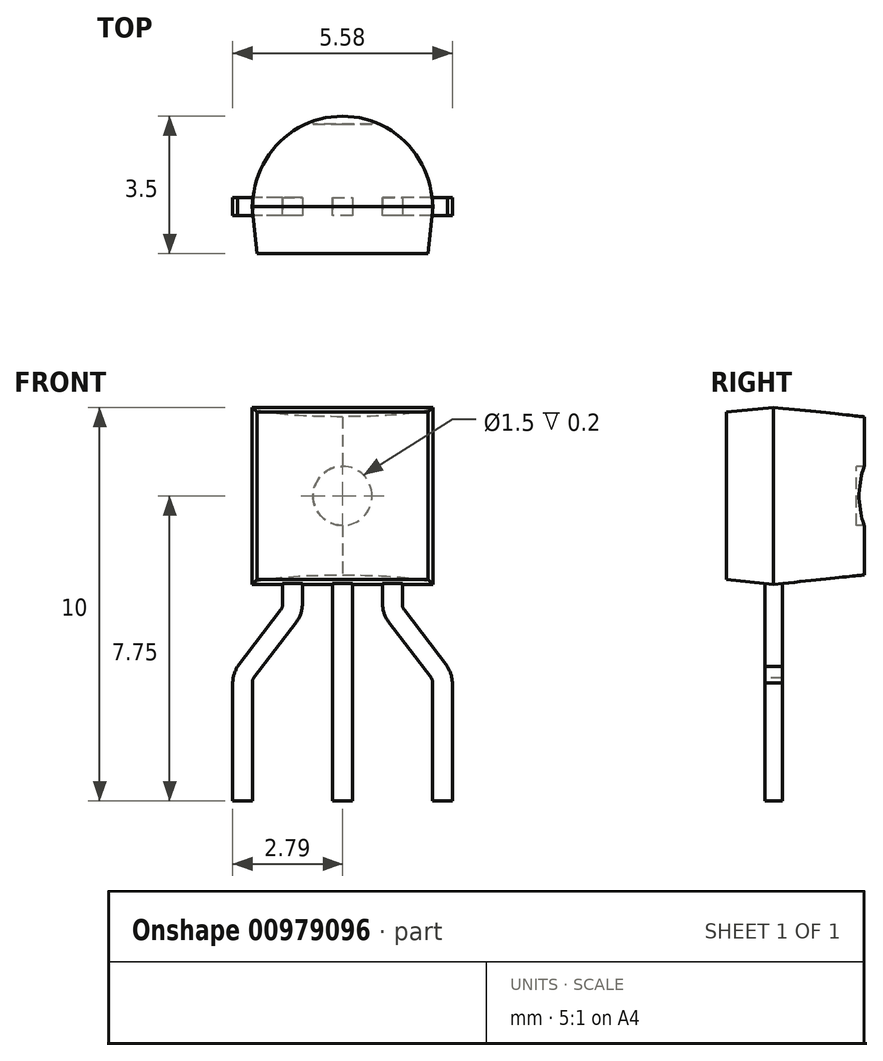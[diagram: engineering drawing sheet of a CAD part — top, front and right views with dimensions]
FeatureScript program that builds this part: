
annotation { "Feature Type Name" : "Feature", "Feature Type Description" : "" }
export const myFeature = defineFeature(function(context is Context, id is Id, definition is map)
    precondition{}
    {
        {
            assignVariable(context, id + "F0", {"name" : "A2", "anyValue" : 1.2});
        }
        {
            assignVariable(context, id + "F1", {"name" : "D", "anyValue" : 4.6});
        }
        {
            assignVariable(context, id + "F2", {"name" : "h", "anyValue" : 0.2});
        }
        {
            assignVariable(context, id + "F3", {"name" : "L1", "anyValue" : 3});
        }
        {
            var Q0;
            Q0=qCreatedBy(makeId("Front.planeOp"),FACE);
            var sketch = newSketch(context, id + "F4", { "sketchPlane" : qUnion([Q0])});
            skLineSegment(sketch, "E0.bottom", {"start": v(2.3, 0) * mm, "end": v(-2.3, 0) * mm});
            skLineSegment(sketch, "E0.top", {"start": v(2.3, 4.5) * mm, "end": v(-2.3, 4.5) * mm});
            skLineSegment(sketch, "E0.left", {"start": v(2.3, 0) * mm, "end": v(2.3, 4.5) * mm});
            skLineSegment(sketch, "E0.right", {"start": v(-2.3, 0) * mm, "end": v(-2.3, 4.5) * mm});
            skPoint(sketch, "E0.middle", {"position": v(0, 2.25) * mm});
            skSolve(sketch);
        }
        {
            var Q0;
            Q0=makeQuery(id+"F4.imprint","IMPRINT",FACE,{"disambiguationData":[TD([[makeQuery(id+"F4.imprint","IMPRINT",EDGE,{"derivedFrom":sQuery(id+"F4.wireOp",EDGE,"E0.bottom")}),-1.0]])]});
            extrude(context, id + "F5", {"entities" : qUnion([Q0]), "depth" : getVariable(context, 'A2') * mm, "offsetDistance" : 25 * mm, "hasDraft" : true, "draftAngle" : 6 * degree, "draftPullDirection" : true, "hasSecondDirection" : true, "secondDirectionOppositeDirection" : true, "secondDirectionDepth" : getVariable(context, 'D') / 2 * mm, "hasSecondDirectionDraft" : true, "secondDirectionDraftAngle" : 6 * degree, "secondDirectionDraftPullDirection" : true});
        }
        {
            var Q0;
            Q0=makeQuery(id+"F5.opExtrude","CAP_EDGE",EDGE,{"disambiguationData":[OSD([sQuery(id+"F4.wireOp",EDGE,"E0.right")])],"isStart":true});
            var Q1;
            Q1=makeQuery(id+"F5.opExtrude","CAP_EDGE",EDGE,{"disambiguationData":[OSD([sQuery(id+"F4.wireOp",EDGE,"E0.left")])],"isStart":true});
            fillet(context, id + "F6", {"entities" : qUnion([Q0, Q1]), "radius" : getVariable(context, 'D') / 2 * mm, "tangentPropagation" : true, "allowEdgeOverflow" : false});
        }
        {
            var Q0;
            Q0=makeQuery(id+"F5.opExtrude","CAP_FACE",FACE,{"disambiguationData":[OSD([sQuery(id+"F4.wireOp",EDGE,"E0.bottom"),sQuery(id+"F4.wireOp",EDGE,"E0.top"),sQuery(id+"F4.wireOp",EDGE,"E0.left"),sQuery(id+"F4.wireOp",EDGE,"E0.right")])],"isStart":false});
            var sketch = newSketch(context, id + "F7", { "sketchPlane" : qUnion([Q0])});
            skCircle(sketch, "E1", {"center": v(0, 2.25) * mm, "radius": 0.75 * mm});
            skPoint(sketch, "E1.centerSnap0", {"position": v(2.17, 2.25) * mm});
            skSolve(sketch);
        }
        {
            var Q0;
            Q0=makeQuery(id+"F7.imprint","IMPRINT",FACE,{"disambiguationData":[TD([[makeQuery(id+"F7.imprint","IMPRINT",EDGE,{"derivedFrom":sQuery(id+"F7.wireOp",EDGE,"E1")}),1.0]])]});
            extrude(context, id + "F8", {"entities" : qUnion([Q0]), "operationType" : NewBodyOperationType.REMOVE, "endBound" : BoundingType.THROUGH_ALL, "oppositeDirection" : true, "depth" : 25 * mm, "offsetDistance" : 25 * mm, "hasSecondDirection" : true, "secondDirectionOppositeDirection" : true, "secondDirectionDepth" : (getVariable(context, 'D') / 2 + getVariable(context, 'A2') - getVariable(context, 'h')) * mm});
        }
        {
            var Q0;
            Q0=qCreatedBy(makeId("Front.planeOp"),FACE);
            var sketch = newSketch(context, id + "F9", { "sketchPlane" : qUnion([Q0])});
            skLineSegment(sketch, "E2", {"start": v(0, 2.25) * mm, "end": v(-1.27, 2.25) * mm});
            skLineSegment(sketch, "E3", {"start": v(-2.54, -2.5) * mm, "end": v(-2.54, -5.5) * mm});
            skLineSegment(sketch, "E4", {"start": v(0, 2.25) * mm, "end": v(0, -5.5) * mm, "construction": true});
            skPoint(sketch, "E5.visualSharp", {"position": v(-2.54, -2.5) * mm});
            skArc(sketch, "E5.filletArc", {"start": v(-2.46, -2.23) * mm, "mid": v(-2.52, -2.36) * mm, "end": v(-2.54, -2.5) * mm});
            skLineSegment(sketch, "E6.MirrorCS", {"start": v(0, 2.25) * mm, "end": v(1.27, 2.25) * mm});
            skLineSegment(sketch, "E7.MirrorCS", {"start": v(1.27, 2.25) * mm, "end": v(1.27, -0.5) * mm});
            skLineSegment(sketch, "E8.MirrorCS", {"start": v(1.37, -0.8) * mm, "end": v(2.46, -2.23) * mm});
            skLineSegment(sketch, "E9.MirrorCS", {"start": v(2.54, -2.5) * mm, "end": v(2.54, -5.5) * mm});
            skArc(sketch, "E10.MirrorCS", {"start": v(2.46, -2.23) * mm, "mid": v(2.52, -2.36) * mm, "end": v(2.54, -2.5) * mm});
            skPoint(sketch, "E11.visualSharp", {"position": v(1.27, -0.67) * mm});
            skArc(sketch, "E11.filletArc", {"start": v(1.27, -0.5) * mm, "mid": v(1.3, -0.66) * mm, "end": v(1.37, -0.8) * mm});
            skLineSegment(sketch, "E12.MirrorCS", {"start": v(-1.27, 2.25) * mm, "end": v(-1.27, -0.5) * mm});
            skLineSegment(sketch, "E13.MirrorCS", {"start": v(-1.37, -0.8) * mm, "end": v(-2.46, -2.23) * mm});
            skArc(sketch, "E14.MirrorCS", {"start": v(-1.27, -0.5) * mm, "mid": v(-1.3, -0.66) * mm, "end": v(-1.37, -0.8) * mm});
            skSolve(sketch);
        }
        {
            var Q0;
            Q0=qCreatedBy(makeId("Right.planeOp"),FACE);
            var sketch = newSketch(context, id + "F10", { "sketchPlane" : qUnion([Q0])});
            skLineSegment(sketch, "E15", {"start": v(0, 2.25) * mm, "end": v(0, -0.5) * mm});
            skLineSegment(sketch, "E16", {"start": v(0, -0.5) * mm, "end": v(0, -2.5) * mm});
            skLineSegment(sketch, "E17", {"start": v(0, -2.5) * mm, "end": v(0, -5.5) * mm});
            skPoint(sketch, "E18.visualSharp", {"position": v(0, -0.38) * mm});
            skLineSegment(sketch, "E18.filletArc", {"start": v(0, -0.5) * mm, "end": v(0, -0.5) * mm});
            skPoint(sketch, "E19.visualSharp", {"position": v(0, -2.64) * mm});
            skLineSegment(sketch, "E19.filletArc", {"start": v(0, -2.5) * mm, "end": v(0, -2.5) * mm});
            skSolve(sketch);
        }
        {
            var Q0;
            Q0=qCreatedBy(makeId("Top.planeOp"),FACE);
            var sketch = newSketch(context, id + "F11", { "sketchPlane" : qUnion([Q0])});
            skLineSegment(sketch, "E20.bottom", {"start": v(-0.25, 0.23) * mm, "end": v(0.25, 0.23) * mm});
            skLineSegment(sketch, "E20.top", {"start": v(-0.25, -0.23) * mm, "end": v(0.25, -0.23) * mm});
            skLineSegment(sketch, "E20.left", {"start": v(-0.25, 0.23) * mm, "end": v(-0.25, -0.23) * mm});
            skLineSegment(sketch, "E20.right", {"start": v(0.25, 0.23) * mm, "end": v(0.25, -0.23) * mm});
            skPoint(sketch, "E20.middle", {"position": v(0, 0) * mm});
            skLineSegment(sketch, "E21.bottom", {"start": v(1.02, 0.23) * mm, "end": v(1.52, 0.23) * mm});
            skLineSegment(sketch, "E21.top", {"start": v(1.02, -0.22) * mm, "end": v(1.52, -0.22) * mm});
            skLineSegment(sketch, "E21.left", {"start": v(1.02, 0.23) * mm, "end": v(1.02, -0.22) * mm});
            skLineSegment(sketch, "E21.right", {"start": v(1.52, 0.23) * mm, "end": v(1.52, -0.22) * mm});
            skPoint(sketch, "E21.middle", {"position": v(1.27, 0) * mm});
            skSolve(sketch);
        }
        {
            var Q0;
            Q0=makeQuery(id+"F11.imprint","IMPRINT",FACE,{"disambiguationData":[TD([[makeQuery(id+"F11.imprint","IMPRINT",EDGE,{"derivedFrom":sQuery(id+"F11.wireOp",EDGE,"E21.bottom")}),-1.0]])]});
            var Q1;
            Q1=sQuery(id+"F9.wireOp",EDGE,"E7.MirrorCS");
            var Q2;
            Q2=sQuery(id+"F9.wireOp",EDGE,"E8.MirrorCS");
            var Q3;
            Q3=sQuery(id+"F9.wireOp",EDGE,"E9.MirrorCS");
            var Q4;
            Q4=sQuery(id+"F9.wireOp",EDGE,"E2");
            var Q5;
            Q5=sQuery(id+"F9.wireOp",EDGE,"E6.MirrorCS");
            var Q6;
            Q6=sQuery(id+"F9.wireOp",EDGE,"E12.MirrorCS");
            var Q7;
            Q7=sQuery(id+"F9.wireOp",EDGE,"E13.MirrorCS");
            var Q8;
            Q8=sQuery(id+"F9.wireOp",EDGE,"E3");
            var Q9;
            Q9=sQuery(id+"F9.wireOp",EDGE,"E11.filletArc");
            var Q10;
            Q10=sQuery(id+"F9.wireOp",EDGE,"E10.MirrorCS");
            var Q11;
            Q11=sQuery(id+"F9.wireOp",EDGE,"E14.MirrorCS");
            var Q12;
            Q12=sQuery(id+"F9.wireOp",EDGE,"E5.filletArc");
            sweep(context, id + "F12", {"profiles" : qUnion([Q0]), "path" : qUnion([Q1, Q2, Q3, Q4, Q5, Q6, Q7, Q8, Q9, Q10, Q11, Q12])});
        }
        {
            var Q0;
            Q0=makeQuery(id+"F11.imprint","IMPRINT",FACE,{"disambiguationData":[TD([[makeQuery(id+"F11.imprint","IMPRINT",EDGE,{"derivedFrom":sQuery(id+"F11.wireOp",EDGE,"E20.bottom")}),-1.0]])]});
            var Q1;
            Q1=sQuery(id+"F10.wireOp",EDGE,"E18.filletArc");
            var Q2;
            Q2=sQuery(id+"F10.wireOp",EDGE,"E15");
            var Q3;
            Q3=sQuery(id+"F10.wireOp",EDGE,"E19.filletArc");
            var Q4;
            Q4=sQuery(id+"F10.wireOp",EDGE,"E16");
            var Q5;
            Q5=sQuery(id+"F10.wireOp",EDGE,"E17");
            sweep(context, id + "F13", {"operationType" : NewBodyOperationType.ADD, "profiles" : qUnion([Q0]), "path" : qUnion([Q1, Q2, Q3, Q4, Q5])});
        }
        {
            var Q0;
            Q0=makeQuery(id+"F5.opExtrude","CAP_FACE",FACE,{"disambiguationData":[OSD([sQuery(id+"F4.wireOp",EDGE,"E0.bottom"),sQuery(id+"F4.wireOp",EDGE,"E0.top"),sQuery(id+"F4.wireOp",EDGE,"E0.left"),sQuery(id+"F4.wireOp",EDGE,"E0.right")])],"isStart":false});
            extrude(context, id + "F14", {"entities" : qUnion([Q0]), "oppositeDirection" : true, "depth" : 0.2 * mm, "offsetDistance" : 25 * mm, "hasSecondDirection" : true, "secondDirectionOppositeDirection" : true, "secondDirectionDepth" : 0.1 * mm});
        }
        {
            var Q0;
            Q0=makeQuery(id+"F14.opExtrude","CAP_FACE",FACE,{"disambiguationData":[OSD([sQuery(id+"F4.wireOp",EDGE,"E0.bottom"),sQuery(id+"F4.wireOp",EDGE,"E0.top"),sQuery(id+"F4.wireOp",EDGE,"E0.left"),sQuery(id+"F4.wireOp",EDGE,"E0.right")])],"isStart":true});
            var sketch = newSketch(context, id + "F15", { "sketchPlane" : qUnion([Q0])});
            skText(sketch, "E22", { "text": "2N", "fontName": "Arimo-Regular.ttf"});
            skText(sketch, "E23", { "text": "5551", "fontName": "Arimo-Regular.ttf"});
            skText(sketch, "E24", { "text": "B001", "fontName": "Arimo-Regular.ttf"});
            skLineSegment(sketch, "E25", {"start": v(-1.3, 0.65) * mm, "end": v(-1.3, 0.13) * mm, "construction": true});
            skLineSegment(sketch, "E26", {"start": v(-1.3, 3.85) * mm, "end": v(-1.3, 4.37) * mm, "construction": true});
            skLineSegment(sketch, "E27", {"start": v(-1.3, 3.05) * mm, "end": v(-1.3, 2.65) * mm, "construction": true});
            skLineSegment(sketch, "E28", {"start": v(-1.3, 1.85) * mm, "end": v(-1.3, 1.45) * mm, "construction": true});
            skLineSegment(sketch, "E29", {"start": v(-2.17, 2.25) * mm, "end": v(-1.3, 2.25) * mm, "construction": true});
            skLineSegment(sketch, "E30", {"start": v(0, 0.13) * mm, "end": v(0, 0.65) * mm, "construction": true});
            const initialGuessF15  = {"E22": [-0.0013, 0.00305, 1, 0, 0.0008], "E23": [-0.0013, 0.00185, 1, 0, 0.0008], "E24": [-0.0013, 0.00065, 1, 0, 0.0008]};
            skSetInitialGuess(sketch, initialGuessF15);
            skSolve(sketch);
        }
        {
            var Q0;
            Q0 = qSketchRegion(id + "F15", true);
            extrude(context, id + "F16", {"entities" : qUnion([Q0]), "operationType" : NewBodyOperationType.ADD, "depth" : 0.1 * mm, "offsetDistance" : 25 * mm});
        }
        {
            var Q0;
            Q0=makeQuery(id+"F12.opSweep","CAP_FACE",FACE,{"disambiguationData":[OSD([sQuery(id+"F9.wireOp",VERTEX,"E3.end"),sQuery(id+"F11.wireOp",EDGE,"E21.bottom"),sQuery(id+"F11.wireOp",EDGE,"E21.top"),sQuery(id+"F11.wireOp",EDGE,"E21.left"),sQuery(id+"F11.wireOp",EDGE,"E21.right")])],"isStart":false});
            cPlane(context, id + "F17", {"entities" : qUnion([Q0]), "cplaneType" : CPlaneType.OFFSET, "offset" : getVariable(context, 'L1') * mm, "oppositeDirection" : true, "width" : 150 * mm, "height" : 150 * mm});
        }
    });
